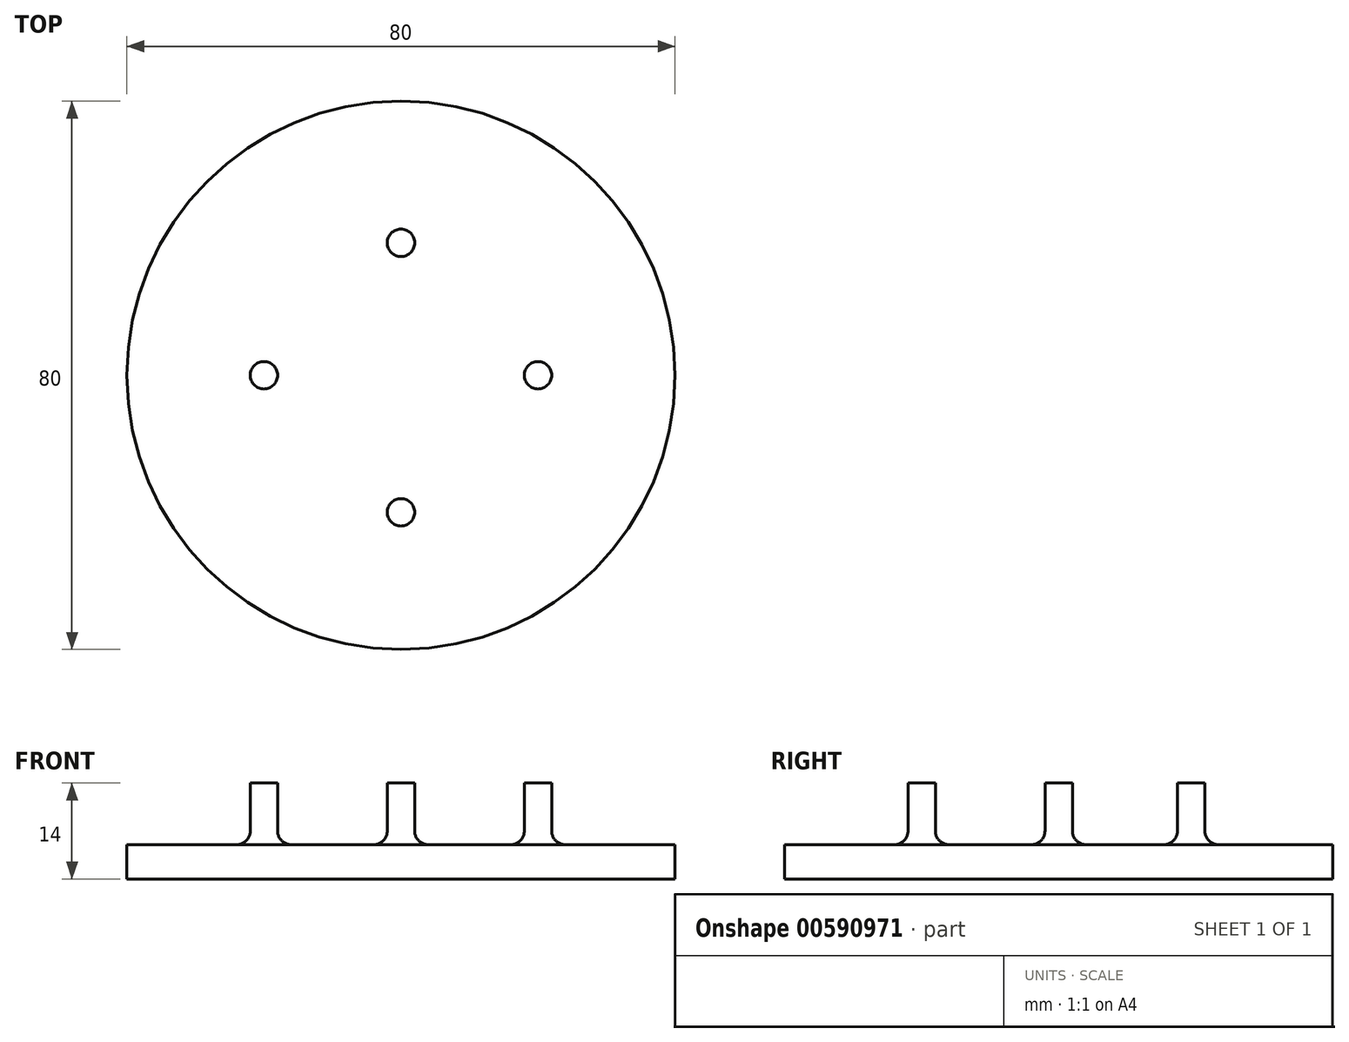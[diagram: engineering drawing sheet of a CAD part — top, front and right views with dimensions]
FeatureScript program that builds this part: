
annotation { "Feature Type Name" : "Feature", "Feature Type Description" : "" }
export const myFeature = defineFeature(function(context is Context, id is Id, definition is map)
    precondition{}
    {
        {
            var Q0;
            Q0=qCreatedBy(makeId("Top.planeOp"),FACE);
            var sketch = newSketch(context, id + "F0", { "sketchPlane" : qUnion([Q0])});
            skCircle(sketch, "E0", {"center": v(0, 0) * mm, "radius": 40 * mm});
            skSolve(sketch);
        }
        {
            var Q0;
            Q0=makeQuery(id+"F0.imprint","IMPRINT",FACE,{"disambiguationData":[TD([[makeQuery(id+"F0.imprint","IMPRINT",EDGE,{"derivedFrom":sQuery(id+"F0.wireOp",EDGE,"E0")}),1.0]])]});
            var sketch = newSketch(context, id + "F1", { "sketchPlane" : qUnion([Q0])});
            skCircle(sketch, "E1", {"center": v(0, 0) * mm, "radius": 40 * mm, "construction": true});
            skLineSegment(sketch, "E2", {"start": v(0, 0) * mm, "end": v(40, 0) * mm, "construction": true});
            skLineSegment(sketch, "E3", {"start": v(0, 0) * mm, "end": v(0, 40) * mm, "construction": true});
            skLineSegment(sketch, "E4", {"start": v(0, 0) * mm, "end": v(-40, 0) * mm, "construction": true});
            skLineSegment(sketch, "E5", {"start": v(0, 0) * mm, "end": v(0, -40) * mm, "construction": true});
            skCircle(sketch, "E6", {"center": v(0, 19.33) * mm, "radius": 2 * mm});
            skCircle(sketch, "E7", {"center": v(-20, 0) * mm, "radius": 2 * mm});
            skCircle(sketch, "E8", {"center": v(20, 0) * mm, "radius": 2 * mm});
            skCircle(sketch, "E9", {"center": v(0, -20) * mm, "radius": 2 * mm});
            skSolve(sketch);
        }
        {
            var Q0;
            Q0=qSketchRegion(id+"F1",true);
            extrude(context, id + "F2", {"entities" : qUnion([Q0]), "depth" : 14 * mm});
        }
        {
            var Q0;
            Q0=qSketchRegion(id+"F0",true);
            extrude(context, id + "F3", {"entities" : qUnion([Q0]), "depth" : 5 * mm});
        }
        {
            var Q0;
            Q0=makeQuery(id+"F3.opExtrude","SWEPT_BODY",BODY,{"disambiguationData":[OSD([sQuery(id+"F0.wireOp",EDGE,"E0")])]});
            var Q1;
            Q1=makeQuery(id+"F2.opExtrude","SWEPT_BODY",BODY,{"disambiguationData":[OSD([sQuery(id+"F1.wireOp",EDGE,"E7")])]});
            var Q2;
            Q2=makeQuery(id+"F2.opExtrude","SWEPT_BODY",BODY,{"disambiguationData":[OSD([sQuery(id+"F1.wireOp",EDGE,"E6")])]});
            var Q3;
            Q3=makeQuery(id+"F2.opExtrude","SWEPT_BODY",BODY,{"disambiguationData":[OSD([sQuery(id+"F1.wireOp",EDGE,"E9")])]});
            var Q4;
            Q4=makeQuery(id+"F2.opExtrude","SWEPT_BODY",BODY,{"disambiguationData":[OSD([sQuery(id+"F1.wireOp",EDGE,"E8")])]});
            booleanBodies(context, id + "F4", {"operationType" : BooleanOperationType.UNION, "tools" : qUnion([Q0, Q1, Q2, Q3, Q4])});
        }
        {
            var Q0;
            Q0=makeQuery(id+"F4.opBoolean","INTERSECT",EDGE,{"derivedFrom":[makeQuery(id+"F2.opExtrude","SWEPT_FACE",FACE,{"disambiguationData":[OSD([sQuery(id+"F1.wireOp",EDGE,"E9")])]}),makeQuery(id+"F3.opExtrude","CAP_FACE",FACE,{"disambiguationData":[OSD([sQuery(id+"F0.wireOp",EDGE,"E0")])],"isStart":false})]});
            var Q1;
            Q1=makeQuery(id+"F4.opBoolean","INTERSECT",EDGE,{"derivedFrom":[makeQuery(id+"F2.opExtrude","SWEPT_FACE",FACE,{"disambiguationData":[OSD([sQuery(id+"F1.wireOp",EDGE,"E7")])]}),makeQuery(id+"F3.opExtrude","CAP_FACE",FACE,{"disambiguationData":[OSD([sQuery(id+"F0.wireOp",EDGE,"E0")])],"isStart":false})]});
            var Q2;
            Q2=makeQuery(id+"F4.opBoolean","INTERSECT",EDGE,{"derivedFrom":[makeQuery(id+"F2.opExtrude","SWEPT_FACE",FACE,{"disambiguationData":[OSD([sQuery(id+"F1.wireOp",EDGE,"E8")])]}),makeQuery(id+"F3.opExtrude","CAP_FACE",FACE,{"disambiguationData":[OSD([sQuery(id+"F0.wireOp",EDGE,"E0")])],"isStart":false})]});
            var Q3;
            Q3=makeQuery(id+"F4.opBoolean","INTERSECT",EDGE,{"derivedFrom":[makeQuery(id+"F2.opExtrude","SWEPT_FACE",FACE,{"disambiguationData":[OSD([sQuery(id+"F1.wireOp",EDGE,"E6")])]}),makeQuery(id+"F3.opExtrude","CAP_FACE",FACE,{"disambiguationData":[OSD([sQuery(id+"F0.wireOp",EDGE,"E0")])],"isStart":false})]});
            fillet(context, id + "F5", {"entities" : qUnion([Q0, Q1, Q2, Q3]), "radius" : 2 * mm, "tangentPropagation" : true, "allowEdgeOverflow" : false});
        }
    });
